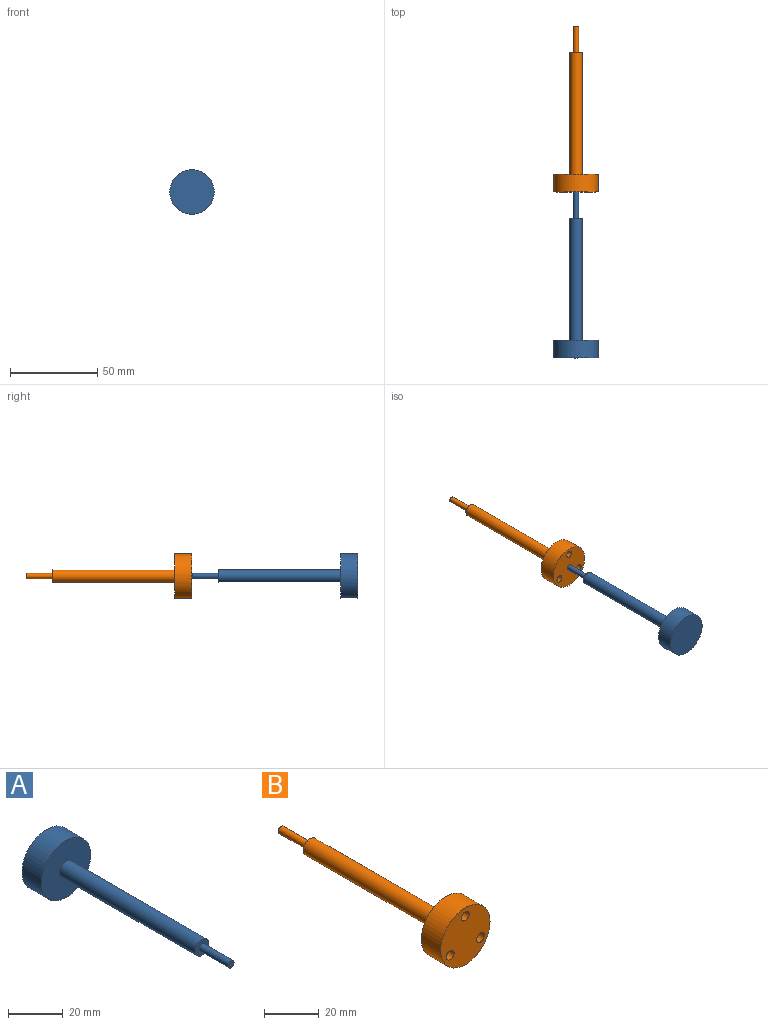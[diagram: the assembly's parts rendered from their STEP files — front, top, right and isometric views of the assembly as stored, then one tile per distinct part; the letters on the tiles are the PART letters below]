
ASSEMBLY  parts=2 mates=1
PART A: 7 faces, bbox 25.4x95x25.4 mm
  f0: cylinder r=12.7mm len=25.4mm, axis (0,1,0), area 798mm2, adj f1,f2
  f1: plane 25.4x25.4mm, normal (0,-1,0), area 468.2mm2, adj f0,f3
  f2: plane 25.4x25.4mm, normal (0,1,0), area 506.7mm2, adj f0
  f3: cylinder r=3.5mm len=70mm, axis (0,1,0), area 1539.4mm2, adj f1,f4
  f4: plane 7x7mm, normal (0,-1,0), area 31.4mm2, adj f3,f5
  f5: cylinder r=1.5mm len=15mm, axis (0,1,0), area 141.4mm2, adj f4,f6
  f6: plane 3x3mm, normal (0,-1,0), area 7.1mm2, adj f5
PART B: 10 faces, bbox 25.4x95x25.4 mm
  f0: plane 25.4x25.4mm, normal (0,-1,0), area 469mm2, adj f1,f7,f8,f9
  f1: cylinder r=12.7mm len=25.4mm, axis (0,-1,0), area 798mm2, adj f0,f2
  f2: plane 25.4x25.4mm, normal (0,1,0), area 430.5mm2, adj f1,f3,f7,f8,f9
  f3: cylinder r=3.5mm len=70mm, axis (0,-1,0), area 1539.4mm2, adj f2,f4
  f4: plane 7x7mm, normal (0,1,0), area 31.4mm2, adj f3,f5
  f5: cylinder r=1.5mm len=15mm, axis (0,-1,0), area 141.4mm2, adj f4,f6
  f6: plane 3x3mm, normal (0,1,0), area 7.1mm2, adj f5
  f7: cylinder r=2mm len=10mm, axis (0,-1,0), area 125.7mm2, adj f0,f2
  f8: cylinder r=2mm len=10mm, axis (0,-1,0), area 125.7mm2, adj f0,f2
  f9: cylinder r=2mm len=10mm, axis (0,-1,0), area 125.7mm2, adj f0,f2
PLACE A rot(axis=(1,0,0),180deg) t=(9.11,-155.77,-27.8)mm
PLACE B t=(9.11,-60.77,-27.8)mm
MATE fastened A.f5 <-> B.f1  axis (0,1,0) through (9.11,-60.77,-27.8)mm
